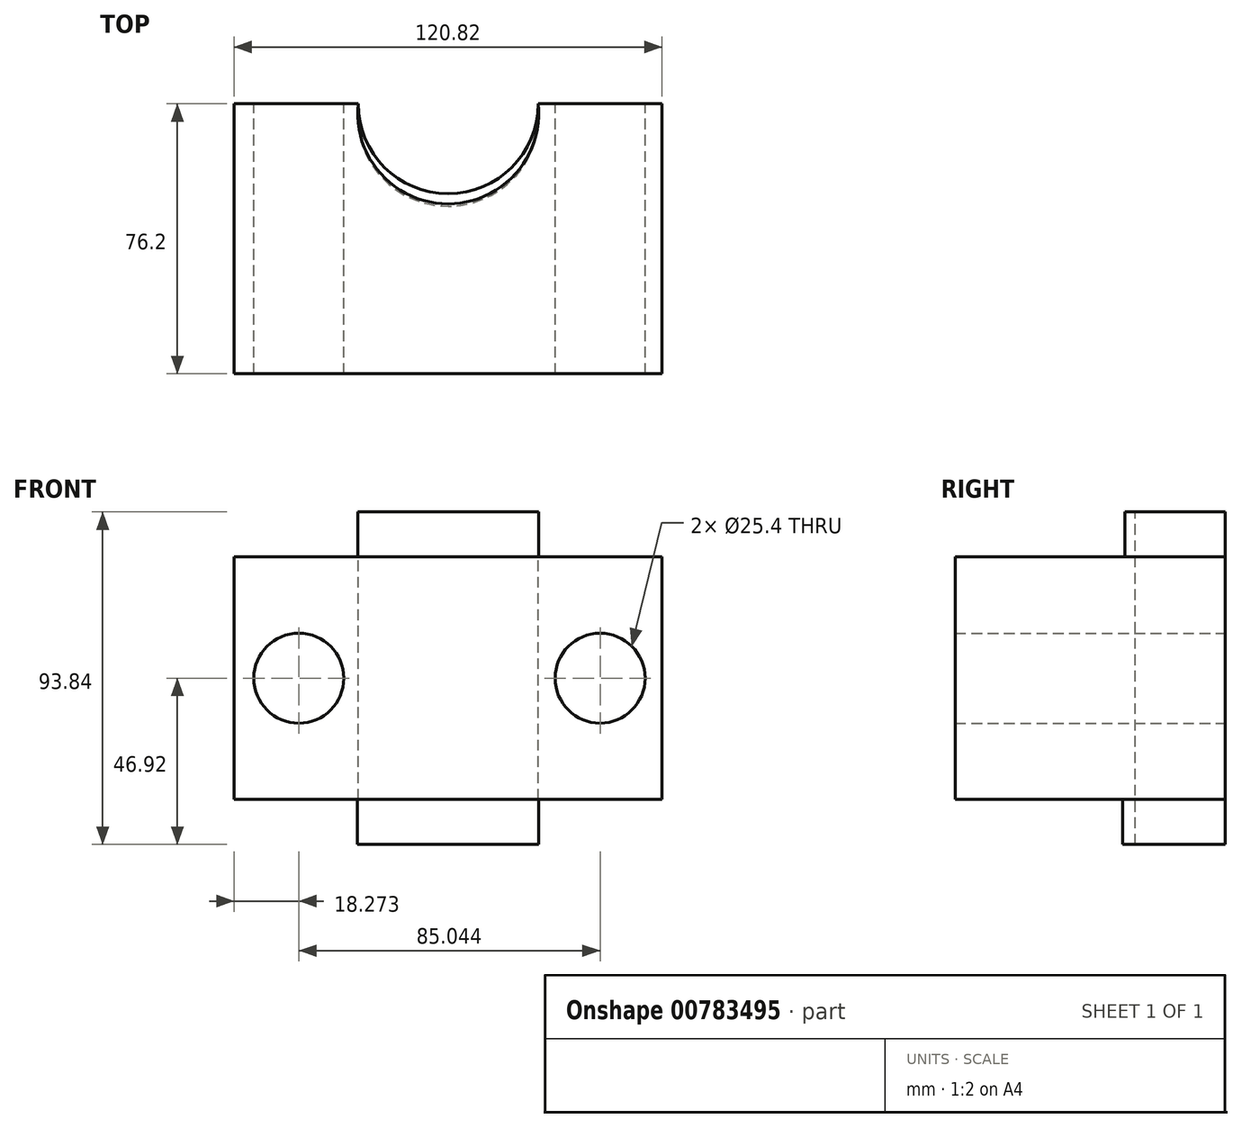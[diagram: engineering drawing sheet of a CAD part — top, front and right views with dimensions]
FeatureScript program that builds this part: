
annotation { "Feature Type Name" : "Feature", "Feature Type Description" : "" }
export const myFeature = defineFeature(function(context is Context, id is Id, definition is map)
    precondition{}
    {
        {
            var Q0;
            Q0=qCreatedBy(makeId("Front.planeOp"),FACE);
            var sketch = newSketch(context, id + "F0", { "sketchPlane" : qUnion([Q0])});
            skLineSegment(sketch, "E0.bottom", {"start": v(60.41, 34.22) * mm, "end": v(-60.41, 34.22) * mm});
            skLineSegment(sketch, "E0.top", {"start": v(60.41, -34.22) * mm, "end": v(-60.41, -34.22) * mm});
            skLineSegment(sketch, "E0.left", {"start": v(60.41, 34.22) * mm, "end": v(60.41, -34.22) * mm});
            skLineSegment(sketch, "E0.right", {"start": v(-60.41, 34.22) * mm, "end": v(-60.41, -34.22) * mm});
            skPoint(sketch, "E0.middle", {"position": v(0, 0) * mm});
            skSolve(sketch);
        }
        {
            var Q0;
            Q0 = qSketchRegion(id + "F0", true);
            var Q1;
            Q1=makeQuery(id+"F0.imprint","IMPRINT",FACE,{"disambiguationData":[TD([[makeQuery(id+"F0.imprint","IMPRINT",EDGE,{"derivedFrom":sQuery(id+"F0.wireOp",EDGE,"E0.bottom")}),1.0]])]});
            extrude(context, id + "F1", {"entities" : qUnion([Q0, Q1]), "depth" : 76.2 * mm, "offsetDistance" : 25.4 * mm});
        }
        {
            var Q0;
            Q0=makeQuery(id+"F1.opExtrude","SWEPT_FACE",FACE,{"disambiguationData":[OSD([sQuery(id+"F0.wireOp",EDGE,"E0.bottom")])]});
            var sketch = newSketch(context, id + "F2", { "sketchPlane" : qUnion([Q0])});
            skPoint(sketch, "E1", {"position": v(0, 0) * mm});
            skSolve(sketch);
        }
        {
            var Q0;
            Q0=sQuery(id+"F2.wireOp",VERTEX,"E1");
            var Q1;
            Q1=makeQuery(id+"F1.opExtrude","SWEPT_BODY",BODY,{"disambiguationData":[OSD([sQuery(id+"F0.wireOp",EDGE,"E0.bottom"),sQuery(id+"F0.wireOp",EDGE,"E0.top"),sQuery(id+"F0.wireOp",EDGE,"E0.left"),sQuery(id+"F0.wireOp",EDGE,"E0.right")])]});
            hole(context, id + "F3", {"style" : HoleStyle.SIMPLE, "endStyle" : HoleEndStyle.THROUGH, "holeDiameter" : 50.8 * mm, "majorDiameter" : 6.35 * mm, "isTappedThrough" : true, "tappedDepth" : 12.7 * mm, "tapClearance" : 3, "locations" : qUnion([Q0]), "scope" : qUnion([Q1])});
        }
        {
            var Q0;
            Q0=makeQuery(id+"F1.opExtrude","SWEPT_FACE",FACE,{"disambiguationData":[OSD([sQuery(id+"F0.wireOp",EDGE,"E0.bottom")])]});
            var sketch = newSketch(context, id + "F4", { "sketchPlane" : qUnion([Q0])});
            skArc(sketch, "E2", {"start": v(-25.4, 0) * mm, "mid": v(0, -28.24) * mm, "end": v(25.4, 0) * mm});
            skSolve(sketch);
        }
        {
            var Q0;
            Q0 = qSketchRegion(id + "F4", true);
            var Q1;
            Q1=makeQuery(id+"F4.imprint","IMPRINT",FACE,{"disambiguationData":[TD([[makeQuery(id+"F4.imprint","IMPRINT",EDGE,{"derivedFrom":sQuery(id+"F4.wireOp",EDGE,"E2")}),1.0]])]});
            extrude(context, id + "F5", {"entities" : qUnion([Q0, Q1]), "operationType" : NewBodyOperationType.ADD, "depth" : 12.7 * mm, "offsetDistance" : 25.4 * mm});
        }
        {
            var Q0;
            Q0=makeQuery(id+"F1.opExtrude","SWEPT_FACE",FACE,{"disambiguationData":[OSD([sQuery(id+"F0.wireOp",EDGE,"E0.top")])]});
            var sketch = newSketch(context, id + "F6", { "sketchPlane" : qUnion([Q0])});
            skArc(sketch, "E3", {"start": v(25.4, 0) * mm, "mid": v(0, 28.91) * mm, "end": v(-25.4, 0) * mm});
            skSolve(sketch);
        }
        {
            var Q0;
            Q0=makeQuery(id+"F6.imprint","IMPRINT",FACE,{"disambiguationData":[TD([[makeQuery(id+"F6.imprint","IMPRINT",EDGE,{"derivedFrom":sQuery(id+"F6.wireOp",EDGE,"E3")}),1.0]])]});
            extrude(context, id + "F7", {"entities" : qUnion([Q0]), "operationType" : NewBodyOperationType.ADD, "depth" : 12.7 * mm, "offsetDistance" : 25.4 * mm});
        }
        {
            var Q0;
            {var subQ0=sQuery(id+"F0.wireOp",EDGE,"E0.bottom");var subQ1=sQuery(id+"F0.wireOp",EDGE,"E0.top");var subQ2=sQuery(id+"F0.wireOp",EDGE,"E0.left");Q0=makeQuery(id+"F3.hole-0.boolean.opBoolean","SPLIT",FACE,{"disambiguationData":[TD([makeQuery(id+"F1.opExtrude","SWEPT_FACE",FACE,{"disambiguationData":[OSD([subQ2])]})])],"derivedFrom":makeQuery(id+"F1.opExtrude","CAP_FACE",FACE,{"disambiguationData":[OSD([subQ0,subQ1,subQ2,sQuery(id+"F0.wireOp",EDGE,"E0.right")])],"isStart":true})});}
            var sketch = newSketch(context, id + "F8", { "sketchPlane" : qUnion([Q0])});
            skPoint(sketch, "E4", {"position": v(-42.9, 0) * mm});
            skPoint(sketch, "E4.positionSnap0", {"position": v(-42.9, 34.22) * mm});
            skPoint(sketch, "E5", {"position": v(42.14, 0) * mm});
            skSolve(sketch);
        }
        {
            var Q0;
            Q0=sQuery(id+"F8.wireOp",VERTEX,"E4");
            var Q1;
            Q1=sQuery(id+"F8.wireOp",VERTEX,"E5");
            var Q2;
            Q2=makeQuery(id+"F1.opExtrude","SWEPT_BODY",BODY,{"disambiguationData":[OSD([sQuery(id+"F0.wireOp",EDGE,"E0.bottom"),sQuery(id+"F0.wireOp",EDGE,"E0.top"),sQuery(id+"F0.wireOp",EDGE,"E0.left"),sQuery(id+"F0.wireOp",EDGE,"E0.right")])]});
            hole(context, id + "F9", {"style" : HoleStyle.SIMPLE, "endStyle" : HoleEndStyle.THROUGH, "holeDiameter" : 25.4 * mm, "majorDiameter" : 6.35 * mm, "isTappedThrough" : true, "tappedDepth" : 12.7 * mm, "tapClearance" : 3, "locations" : qUnion([Q0, Q1]), "scope" : qUnion([Q2])});
        }
    });
